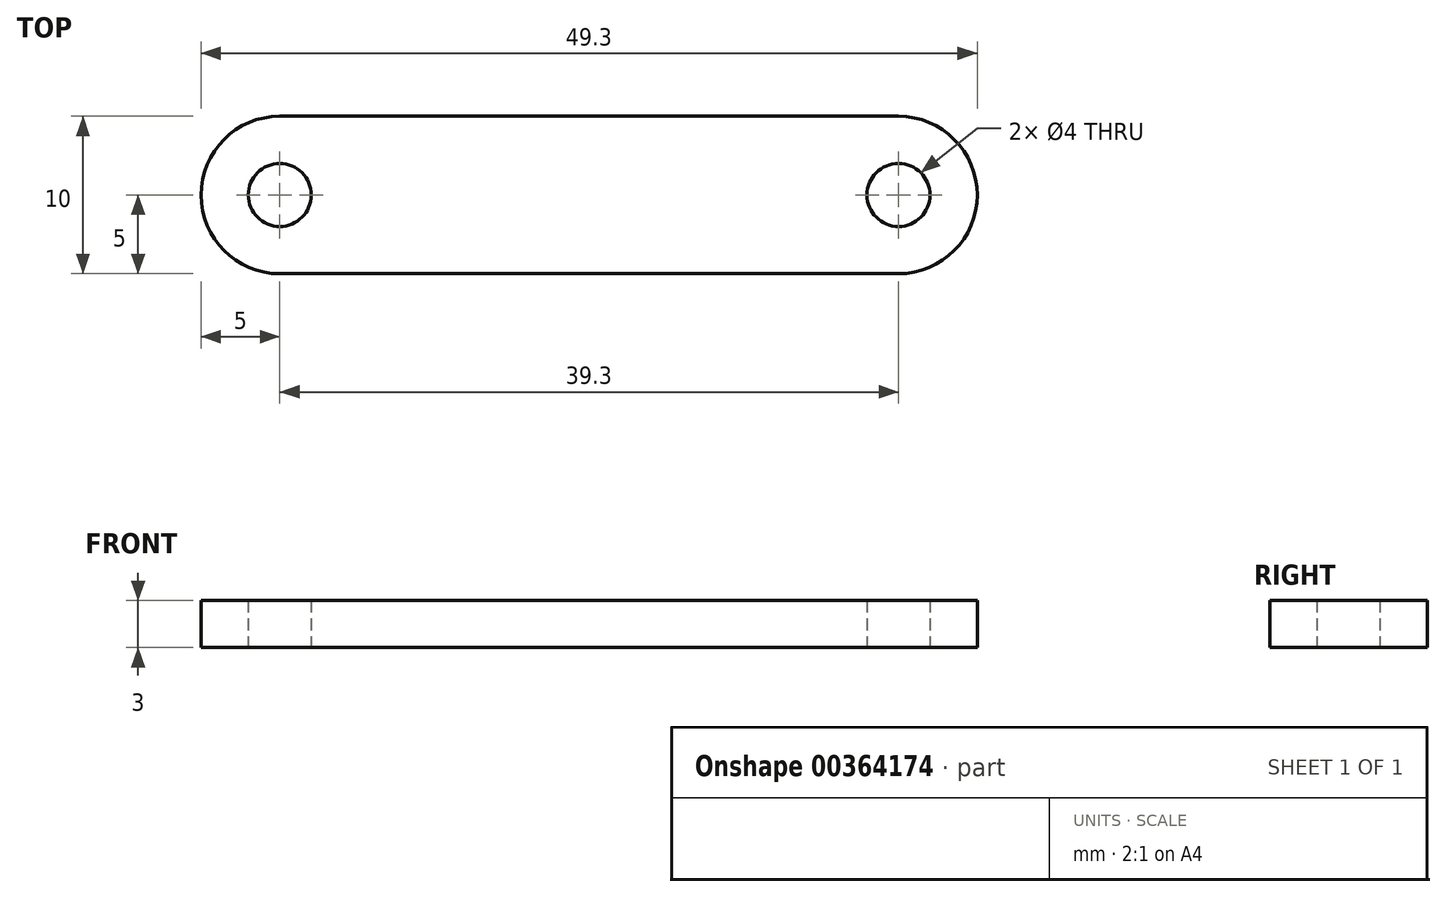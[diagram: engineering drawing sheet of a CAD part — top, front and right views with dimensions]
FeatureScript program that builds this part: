
annotation { "Feature Type Name" : "Feature", "Feature Type Description" : "" }
export const myFeature = defineFeature(function(context is Context, id is Id, definition is map)
    precondition{}
    {
        {
            var Q0;
            Q0=qCreatedBy(makeId("Top.planeOp"),FACE);
            var sketch = newSketch(context, id + "F0", { "sketchPlane" : qUnion([Q0])});
            skLineSegment(sketch, "E0.bottom", {"start": v(19.65, 5) * mm, "end": v(-19.65, 5) * mm});
            skLineSegment(sketch, "E0.top", {"start": v(19.65, -5) * mm, "end": v(-19.65, -5) * mm});
            skPoint(sketch, "E0.middle", {"position": v(0, 0) * mm});
            skCircle(sketch, "E1", {"center": v(-19.65, 0) * mm, "radius": 2 * mm});
            skCircle(sketch, "E2", {"center": v(19.65, 0) * mm, "radius": 2 * mm});
            skArc(sketch, "E3", {"start": v(-19.65, 5) * mm, "mid": v(-24.65, 0) * mm, "end": v(-19.65, -5) * mm});
            skArc(sketch, "E4", {"start": v(19.65, -5) * mm, "mid": v(24.65, 0) * mm, "end": v(19.65, 5) * mm});
            skSolve(sketch);
        }
        {
            var Q0;
            Q0=qSketchRegion(id+"F0",true);
            extrude(context, id + "F1", {"entities" : qUnion([Q0]), "depth" : 3 * mm});
        }
    });
